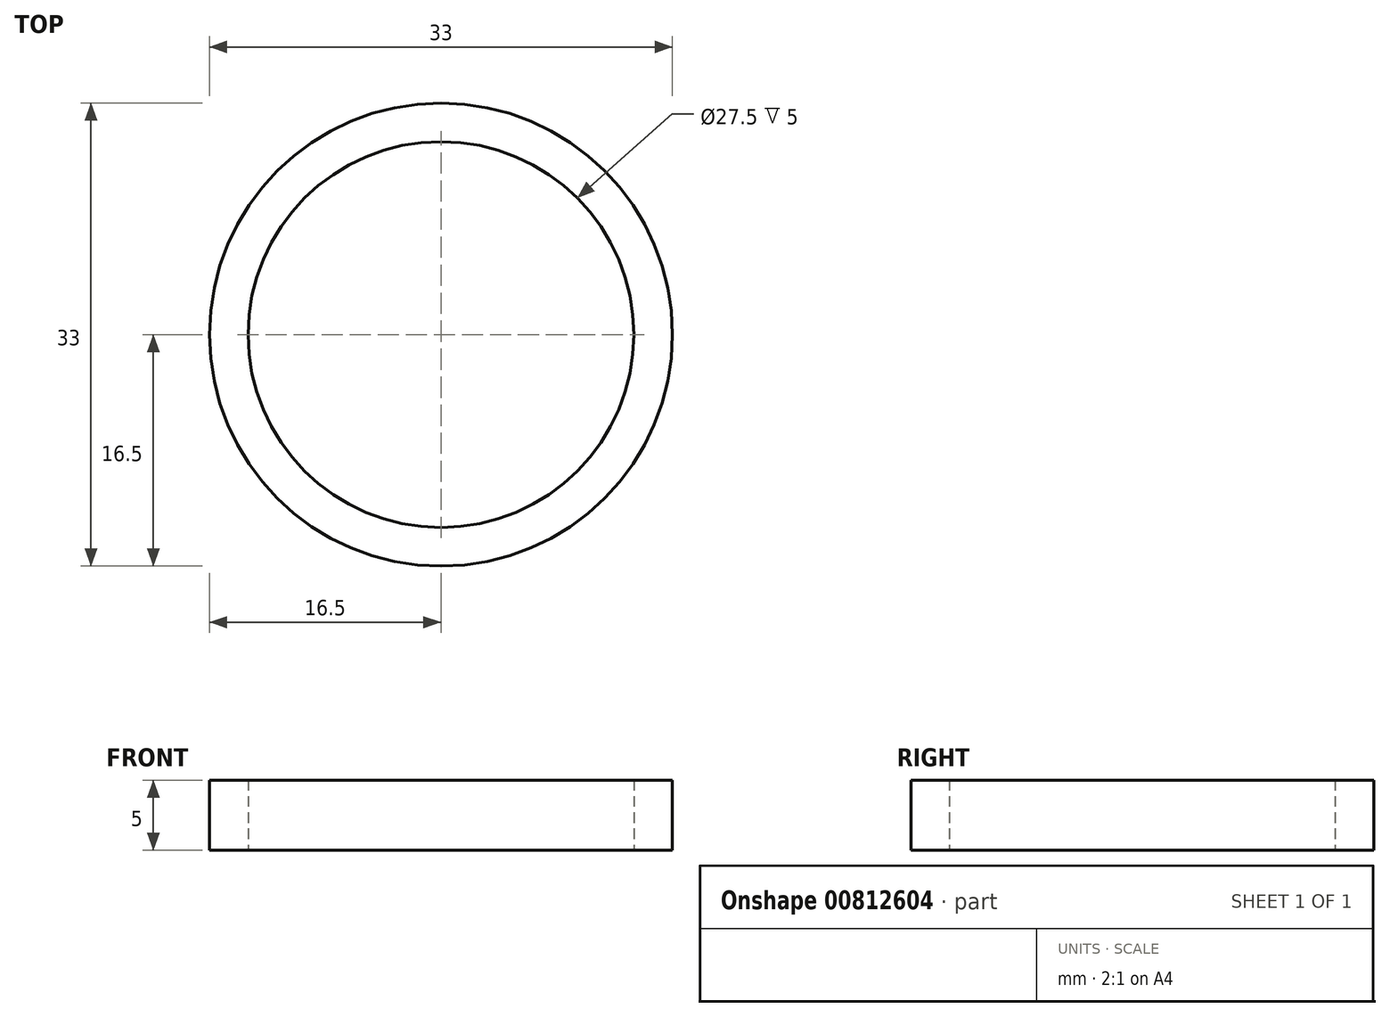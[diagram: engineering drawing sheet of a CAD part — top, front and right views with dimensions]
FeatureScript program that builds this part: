
annotation { "Feature Type Name" : "Feature", "Feature Type Description" : "" }
export const myFeature = defineFeature(function(context is Context, id is Id, definition is map)
    precondition{}
    {
        {
            var Q0;
            Q0=qCreatedBy(makeId("Top.planeOp"),FACE);
            var sketch = newSketch(context, id + "F0", { "sketchPlane" : qUnion([Q0])});
            skCircle(sketch, "E0", {"center": v(0, 0) * mm, "radius": 13.75 * mm});
            skCircle(sketch, "E1", {"center": v(0, 0) * mm, "radius": 16.5 * mm});
            skSolve(sketch);
        }
        {
            var Q0;
            Q0 = qSketchRegion(id + "F0", true);
            extrude(context, id + "F1", {"entities" : qUnion([Q0]), "depth" : 5 * mm, "offsetDistance" : 25 * mm});
        }
    });
